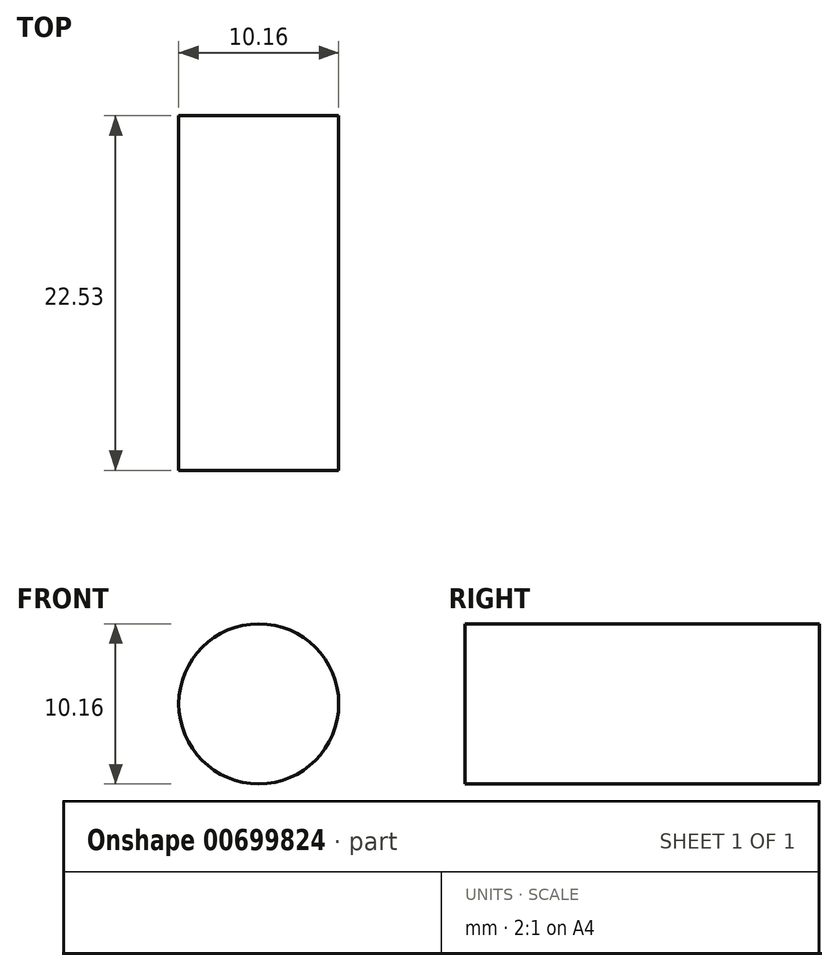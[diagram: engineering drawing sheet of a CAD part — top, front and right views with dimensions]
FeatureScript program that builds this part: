
annotation { "Feature Type Name" : "Feature", "Feature Type Description" : "" }
export const myFeature = defineFeature(function(context is Context, id is Id, definition is map)
    precondition{}
    {
        {
            var Q0;
            Q0=qCreatedBy(makeId("Front.planeOp"),FACE);
            var sketch = newSketch(context, id + "F0", { "sketchPlane" : qUnion([Q0])});
            skCircle(sketch, "E0", {"center": v(0, 0) * mm, "radius": 5.08 * mm});
            skSolve(sketch);
        }
        {
            var Q0;
            Q0=qSketchRegion(id+"F0",true);
            extrude(context, id + "F1", {"entities" : qUnion([Q0]), "depth" : 22.53 * mm});
        }
    });
